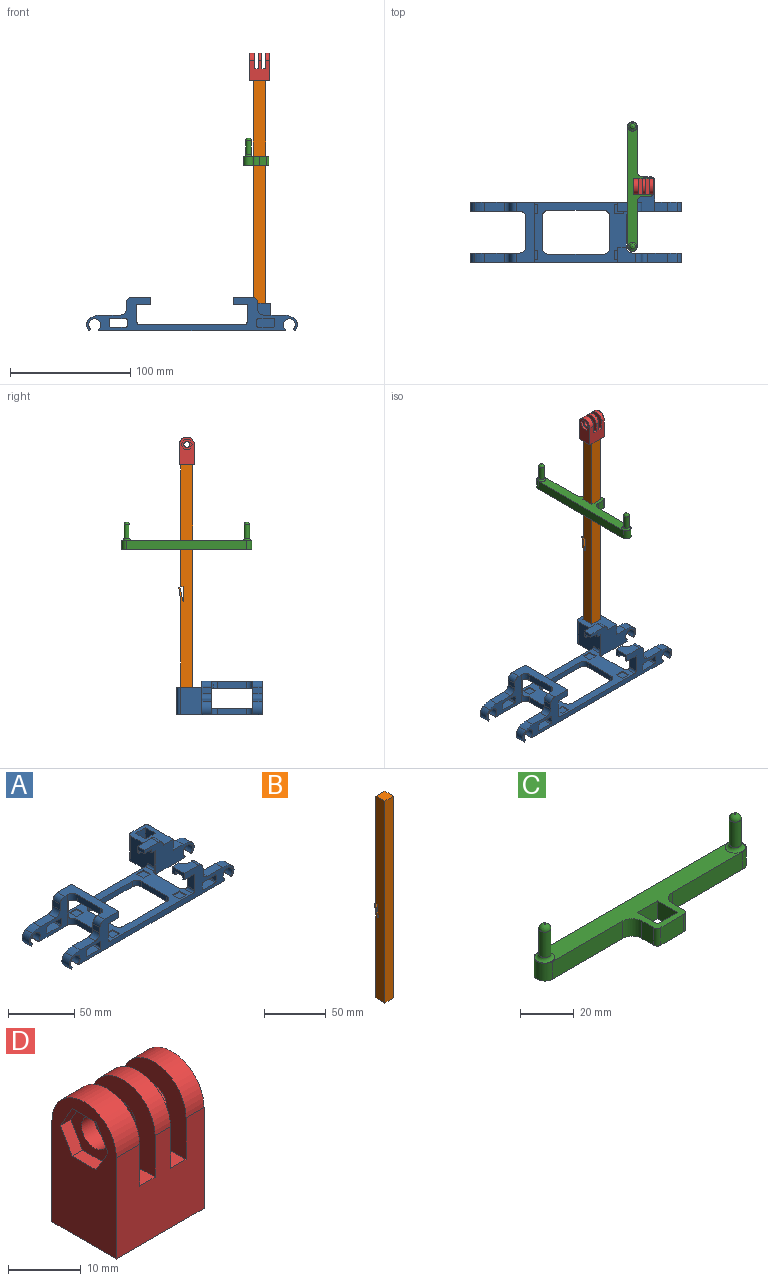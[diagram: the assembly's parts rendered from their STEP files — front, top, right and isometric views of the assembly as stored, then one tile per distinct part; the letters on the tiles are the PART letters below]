
ASSEMBLY  parts=4 mates=3
PART A: 147 faces, bbox 175.5x70.9x28.2 mm
  f0: plane 15x12.6mm, normal (0,0,1), area 154.4mm2, adj f4,f5,f6,f66,f114,f146
  f1: plane 15x7.6mm, normal (0,0,1), area 114mm2, adj f30,f61,f65,f115
  f2: plane 11x7.6mm, normal (0,0,-1), area 39.7mm2, adj f30,f55,f61,f65,f103,f104
  f3: plane 12.6x11mm, normal (0,0,-1), area 67.7mm2, adj f4,f5,f47,f66,f99,f100,f101,f146
  f4: plane 12.6x6mm, normal (-1,0,0), area 53.1mm2, adj f0,f3,f5,f100,f101,f102,f146
  f5: plane 175.5x28.17mm, normal (0,-1,0), area 1536.8mm2, adj f0,f3,f4,f7,f11,f12,f13,f14
  f6: plane 40.95x28.17mm, normal (0,1,0), area 444.6mm2, adj f0,f19,f45,f48,f49,f50,f51,f52
  f7: plane 87.6x50mm, normal (0,0,1), area 2008.8mm2, adj f5,f9,f12,f23,f34,f35,f36,f37
  f8: plane 10.5x7.6mm, normal (0,0,1), area 79.8mm2, adj f10,f56,f65,f69
  f9: plane 133.55x28.17mm, normal (0,1,0), area 998.3mm2, adj f7,f19,f21,f22,f23,f24,f25,f26
  f10: plane 22.25x13.17mm, normal (0,1,0), area 185.6mm2, adj f8,f19,f56,f57,f58,f59,f60,f69
  f11: plane 16.2x7.6mm, normal (0,0,1), area 123.1mm2, adj f5,f14,f39,f117
  f12: cylinder r=2mm len=8.6mm, axis (0,1,0), area 25mm2, adj f5,f7,f13,f41
  f13: plane 15x7.7mm, normal (1,0,0), area 115.5mm2, adj f5,f12,f32,f41
  f14: cylinder r=17.38mm len=8.18mm, axis (0,1,0), area 64.7mm2, adj f5,f11,f15,f39
  f15: cylinder r=6.75mm len=11.13mm, axis (0,1,0), area 100.2mm2, adj f5,f14,f16,f39
  f16: plane 7.6x1.34mm, normal (0.77,0,-0.64), area 13.3mm2, adj f5,f15,f17,f39
  f17: cylinder r=5mm len=10mm, axis (0,1,0), area 189mm2, adj f5,f16,f18,f39
  f18: plane 7.6x0.9mm, normal (-0.82,0,-0.57), area 8.4mm2, adj f5,f17,f19,f39
  f19: plane 155x70.9mm, normal (0,0,-1), area 3670mm2, adj f5,f6,f9,f10,f18,f29,f34,f35
  f20: plane 7.6x5mm, normal (-1,0,0), area 38mm2, adj f5,f39,f117,f118
  f21: plane 50x15mm, normal (0,0,1), area 482.3mm2, adj f5,f9,f33,f39,f40,f41,f43,f44
  f22: plane 16.2x7.6mm, normal (0,0,1), area 123.1mm2, adj f9,f25,f40,f120
  f23: cylinder r=2mm len=8.6mm, axis (0,1,0), area 25mm2, adj f7,f9,f24,f44
  f24: plane 15x7.7mm, normal (1,0,0), area 115.5mm2, adj f9,f23,f32,f44
  f25: cylinder r=17.38mm len=8.18mm, axis (0,1,0), area 64.7mm2, adj f9,f22,f26,f40
  f26: cylinder r=6.75mm len=11.13mm, axis (0,1,0), area 100.2mm2, adj f9,f25,f27,f40
  f27: plane 7.6x1.34mm, normal (0.77,0,-0.64), area 13.3mm2, adj f9,f26,f28,f40
  f28: cylinder r=5mm len=10mm, axis (0,1,0), area 189mm2, adj f9,f27,f29,f40
  f29: plane 7.6x0.9mm, normal (-0.82,0,-0.57), area 8.4mm2, adj f9,f19,f28,f40
  f30: plane 20x6mm, normal (0,1,0), area 105.6mm2, adj f1,f2,f55,f61,f77,f115
  f31: plane 7.6x5mm, normal (-1,0,0), area 38mm2, adj f9,f40,f119,f120
  f32: plane 50x11mm, normal (0,0,-1), area 309mm2, adj f5,f9,f13,f24,f33,f41,f43,f44
  f33: plane 50x6mm, normal (1,0,0), area 255mm2, adj f5,f9,f21,f32,f106,f107,f109,f111
  f34: cylinder r=5mm len=5mm, axis (0,0,1), area 39.3mm2, adj f7,f19,f35,f38
  f35: plane 45.6x5mm, normal (0,1,0), area 228mm2, adj f7,f19,f34,f62
  f36: plane 45.6x5mm, normal (0,-1,0), area 228mm2, adj f7,f19,f37,f63
  f37: cylinder r=5mm len=5mm, axis (0,0,1), area 39.3mm2, adj f7,f19,f36,f38
  f38: plane 26.8x5mm, normal (1,0,0), area 134mm2, adj f7,f19,f34,f37
  f39: plane 40.95x28.17mm, normal (0,1,0), area 444.6mm2, adj f11,f14,f15,f16,f17,f18,f19,f20
  f40: plane 40.95x28.17mm, normal (0,-1,0), area 444.6mm2, adj f19,f21,f22,f25,f26,f27,f28,f29
  f41: cylinder r=5mm len=28mm, axis (0,0,1), area 104.4mm2, adj f7,f12,f13,f19,f21,f32,f39,f42
  f42: plane 24.8x5mm, normal (-1,0,0), area 124mm2, adj f7,f19,f41,f44
  f43: plane 24.8x6mm, normal (-1,0,0), area 148.8mm2, adj f21,f32,f41,f44
  f44: cylinder r=5mm len=28mm, axis (0,0,1), area 104.4mm2, adj f7,f19,f21,f23,f24,f32,f40,f42
  f45: plane 16.2x7.6mm, normal (0,0,1), area 123.1mm2, adj f5,f6,f48,f116
  f46: cylinder r=2mm len=8.6mm, axis (0,1,0), area 25mm2, adj f5,f7,f47,f66
  f47: plane 15x7.7mm, normal (-1,0,0), area 115.5mm2, adj f3,f5,f46,f66
  f48: cylinder r=17.38mm len=8.18mm, axis (0,1,0), area 64.7mm2, adj f5,f6,f45,f49
  f49: cylinder r=6.75mm len=11.13mm, axis (0,1,0), area 100.2mm2, adj f5,f6,f48,f50
  f50: plane 7.6x1.34mm, normal (-0.77,0,-0.64), area 13.3mm2, adj f5,f6,f49,f51
  f51: cylinder r=5mm len=10mm, axis (0,1,0), area 189mm2, adj f5,f6,f50,f52
  f52: plane 7.6x0.9mm, normal (0.82,0,-0.57), area 8.4mm2, adj f5,f6,f19,f51
  f53: plane 7.6x5mm, normal (1,0,0), area 38mm2, adj f5,f6,f114,f116
  f54: cylinder r=2mm len=8.6mm, axis (0,1,0), area 25mm2, adj f7,f9,f55,f68
  f55: plane 25.6x23mm, normal (-1,0,0), area 527.2mm2, adj f2,f9,f19,f30,f54,f68,f72,f77
  f56: cylinder r=17.38mm len=8.18mm, axis (0,1,0), area 64.7mm2, adj f8,f10,f57,f65
  f57: cylinder r=6.75mm len=11.13mm, axis (0,1,0), area 100.2mm2, adj f10,f56,f58,f65
  f58: plane 7.6x1.34mm, normal (-0.77,0,-0.64), area 13.3mm2, adj f10,f57,f59,f65
  f59: cylinder r=5mm len=10mm, axis (0,1,0), area 189mm2, adj f10,f58,f60,f65
  f60: plane 7.6x0.9mm, normal (0.82,0,-0.57), area 8.4mm2, adj f10,f19,f59,f65
  f61: plane 7.6x6mm, normal (-1,0,0), area 28.1mm2, adj f1,f2,f30,f65,f104,f105
  f62: cylinder r=5mm len=5mm, axis (0,0,1), area 39.3mm2, adj f7,f19,f35,f64
  f63: cylinder r=5mm len=5mm, axis (0,0,1), area 39.3mm2, adj f7,f19,f36,f64
  f64: plane 26.8x5mm, normal (-1,0,0), area 134mm2, adj f7,f19,f62,f63
  f65: plane 52.95x28.17mm, normal (0,-1,0), area 699.8mm2, adj f1,f2,f8,f19,f56,f57,f58,f59
  f66: cylinder r=5mm len=28mm, axis (0,0,1), area 104.4mm2, adj f0,f3,f6,f7,f19,f46,f47,f67
  f67: plane 24.8x5mm, normal (1,0,0), area 124mm2, adj f7,f19,f66,f68
  f68: cylinder r=5mm len=22mm, axis (0,0,1), area 57.3mm2, adj f7,f19,f54,f55,f65,f67,f145
  f69: plane 25.5x23mm, normal (1,0,0), area 487.7mm2, adj f8,f10,f19,f65,f70,f77
  f70: cylinder r=3mm len=23mm, axis (0,0,1), area 108.4mm2, adj f19,f69,f71,f77
  f71: plane 23x13.7mm, normal (0,1,0), area 315.1mm2, adj f19,f70,f72,f77
  f72: cylinder r=3mm len=23mm, axis (0,0,1), area 108.4mm2, adj f19,f55,f71,f77
  f73: plane 10.5x10mm, normal (0,1,0), area 105mm2, adj f74,f76,f77,f78
  f74: plane 10.5x10mm, normal (1,0,0), area 105mm2, adj f73,f75,f77,f78
  f75: plane 10.5x10mm, normal (0,-1,0), area 105mm2, adj f74,f76,f77,f78
  f76: plane 10.5x10mm, normal (-1,0,0), area 105mm2, adj f73,f75,f77,f78
  f77: plane 28.5x19.7mm, normal (0,0,1), area 378.9mm2, adj f30,f55,f65,f69,f70,f71,f72,f73
  f78: plane 10.5x10.5mm, normal (0,0,1), area 110.3mm2, adj f73,f74,f75,f76
  f79: plane 7.5x1mm, normal (-1,0,0), area 7.5mm2, adj f7,f80,f82,f83
  f80: plane 7.5x1mm, normal (0,-1,0), area 7.5mm2, adj f7,f79,f81,f83
  f81: plane 7.5x1mm, normal (1,0,0), area 7.5mm2, adj f7,f80,f82,f83
  f82: plane 7.5x1mm, normal (0,1,0), area 7.5mm2, adj f7,f79,f81,f83
  f83: plane 7.5x7.5mm, normal (0,0,1), area 56.2mm2, adj f79,f80,f81,f82
  f84: plane 7.5x1mm, normal (1,0,0), area 7.5mm2, adj f7,f85,f87,f88
  f85: plane 7.5x1mm, normal (0,1,0), area 7.5mm2, adj f7,f84,f86,f88
  f86: plane 7.5x1mm, normal (-1,0,0), area 7.5mm2, adj f7,f85,f87,f88
  f87: plane 7.5x1mm, normal (0,-1,0), area 7.5mm2, adj f7,f84,f86,f88
  f88: plane 7.5x7.5mm, normal (0,0,1), area 56.2mm2, adj f84,f85,f86,f87
  f89: plane 7.5x1mm, normal (0,1,0), area 7.5mm2, adj f7,f90,f92,f93
  f90: plane 7.5x1mm, normal (-1,0,0), area 7.5mm2, adj f7,f89,f91,f93
  f91: plane 7.5x1mm, normal (0,-1,0), area 7.5mm2, adj f7,f90,f92,f93
  f92: plane 7.5x1mm, normal (1,0,0), area 7.5mm2, adj f7,f89,f91,f93
  f93: plane 7.5x7.5mm, normal (0,0,1), area 56.3mm2, adj f89,f90,f91,f92
  f94: plane 7.5x1mm, normal (1,0,0), area 7.5mm2, adj f7,f95,f97,f98
  f95: plane 7.5x1mm, normal (0,1,0), area 7.5mm2, adj f7,f94,f96,f98
  f96: plane 7.5x1mm, normal (-1,0,0), area 7.5mm2, adj f7,f95,f97,f98
  f97: plane 7.5x1mm, normal (0,-1,0), area 7.5mm2, adj f7,f94,f96,f98
  f98: plane 7.5x7.5mm, normal (0,0,1), area 56.2mm2, adj f94,f95,f96,f97
  f99: plane 7.5x3mm, normal (-1,0,0), area 22.5mm2, adj f3,f100,f101,f102
  f100: plane 7.5x3mm, normal (0,-1,0), area 22.5mm2, adj f3,f4,f99,f102
  f101: plane 7.5x3mm, normal (0,1,0), area 22.5mm2, adj f3,f4,f99,f102
  f102: plane 7.5x7.5mm, normal (0,0,-1), area 56.2mm2, adj f4,f99,f100,f101
  f103: plane 5.85x3mm, normal (-1,0,0), area 17.6mm2, adj f2,f65,f104,f105
  f104: plane 7.5x3mm, normal (0,-1,0), area 22.5mm2, adj f2,f61,f103,f105
  f105: plane 7.5x5.85mm, normal (0,0,-1), area 43.9mm2, adj f61,f65,f103,f104
  f106: plane 7.5x3mm, normal (0,1,0), area 22.5mm2, adj f32,f33,f108,f109
  f107: plane 7.5x3mm, normal (0,-1,0), area 22.5mm2, adj f32,f33,f108,f109
  f108: plane 7.5x3mm, normal (1,0,0), area 22.5mm2, adj f32,f106,f107,f109
  f109: plane 7.5x7.5mm, normal (0,0,-1), area 56.2mm2, adj f33,f106,f107,f108
  f110: plane 7.5x3mm, normal (1,0,0), area 22.5mm2, adj f32,f111,f112,f113
  f111: plane 7.5x3mm, normal (0,1,0), area 22.5mm2, adj f32,f33,f110,f113
  f112: plane 7.5x3mm, normal (0,-1,0), area 22.5mm2, adj f32,f33,f110,f113
  f113: plane 7.5x7.5mm, normal (0,0,-1), area 56.2mm2, adj f33,f110,f111,f112
  f114: cylinder r=5mm len=7.6mm, axis (0,-1,0), area 59.7mm2, adj f0,f5,f6,f53
  f115: cylinder r=5mm len=7.6mm, axis (0,-1,0), area 59.7mm2, adj f1,f30,f65,f77
  f116: cylinder r=5mm len=7.6mm, axis (0,-1,0), area 59.7mm2, adj f5,f6,f45,f53
  f117: cylinder r=5mm len=7.6mm, axis (0,-1,0), area 59.7mm2, adj f5,f11,f20,f39
  f118: cylinder r=5mm len=7.6mm, axis (0,-1,0), area 59.7mm2, adj f5,f20,f21,f39
  f119: cylinder r=5mm len=7.6mm, axis (0,-1,0), area 59.7mm2, adj f9,f21,f31,f40
  f120: cylinder r=5mm len=7.6mm, axis (0,-1,0), area 59.7mm2, adj f9,f22,f31,f40
  f121: plane 7.6x5mm, normal (1,0,0), area 38mm2, adj f9,f40,f122,f128
  f122: cylinder r=1mm len=7.6mm, axis (0,-1,0), area 11.9mm2, adj f9,f40,f121,f123
  f123: plane 13x7.6mm, normal (0,0,-1), area 98.8mm2, adj f9,f40,f122,f124
  f124: cylinder r=1mm len=7.6mm, axis (0,-1,0), area 11.9mm2, adj f9,f40,f123,f125
  f125: plane 7.6x5mm, normal (-1,0,0), area 38mm2, adj f9,f40,f124,f126
  f126: cylinder r=1mm len=7.6mm, axis (0,-1,0), area 11.9mm2, adj f9,f40,f125,f127
  f127: plane 13x7.6mm, normal (0,0,1), area 98.8mm2, adj f9,f40,f126,f128
  f128: cylinder r=1mm len=7.6mm, axis (0,-1,0), area 11.9mm2, adj f9,f40,f121,f127
  f129: cylinder r=1mm len=7.6mm, axis (0,-1,0), area 11.9mm2, adj f5,f39,f130,f136
  f130: plane 13x7.6mm, normal (0,0,1), area 98.8mm2, adj f5,f39,f129,f131
  f131: cylinder r=1mm len=7.6mm, axis (0,-1,0), area 11.9mm2, adj f5,f39,f130,f132
  f132: plane 7.6x5mm, normal (-1,0,0), area 38mm2, adj f5,f39,f131,f133
  f133: cylinder r=1mm len=7.6mm, axis (0,-1,0), area 11.9mm2, adj f5,f39,f132,f134
  f134: plane 13x7.6mm, normal (0,0,-1), area 98.8mm2, adj f5,f39,f133,f135
  f135: cylinder r=1mm len=7.6mm, axis (0,-1,0), area 11.9mm2, adj f5,f39,f134,f136
  f136: plane 7.6x5mm, normal (1,0,0), area 38mm2, adj f5,f39,f129,f135
  f137: plane 13x7.6mm, normal (0,0,1), area 98.8mm2, adj f5,f6,f138,f142
  f138: cylinder r=1mm len=7.6mm, axis (0,-1,0), area 11.9mm2, adj f5,f6,f137,f139
  f139: plane 7.6x5mm, normal (-1,0,0), area 38mm2, adj f5,f6,f138,f140
  f140: cylinder r=1mm len=7.6mm, axis (0,-1,0), area 11.9mm2, adj f5,f6,f139,f141
  f141: plane 13x7.6mm, normal (0,0,-1), area 98.8mm2, adj f5,f6,f140,f143
  f142: cylinder r=1mm len=7.6mm, axis (0,-1,0), area 11.9mm2, adj f5,f6,f137,f144
  f143: cylinder r=1mm len=7.6mm, axis (0,-1,0), area 11.9mm2, adj f5,f6,f141,f144
  f144: plane 7.6x5mm, normal (1,0,0), area 38mm2, adj f5,f6,f142,f143
  f145: plane 1x0.1mm, normal (0,0,1), area 0mm2, adj f55,f65,f68
  f146: plane 7x6mm, normal (0,1,0), area 42mm2, adj f0,f3,f4,f66
PART B: 13 faces, bbox 10.1x11.8x200 mm
  f0: plane 81.12x10.1mm, normal (0,1,0), area 819.3mm2, adj f1,f2,f6,f12
  f1: plane 200x11.77mm, normal (1,0,0), area 2009.3mm2, adj f0,f3,f4,f5,f6,f7,f8,f9
  f2: plane 200x11.77mm, normal (-1,0,0), area 2009.3mm2, adj f0,f3,f4,f5,f6,f7,f8,f9
  f3: plane 200x10.1mm, normal (0,-1,0), area 2020mm2, adj f1,f2,f5,f6
  f4: plane 106.39x10.1mm, normal (0,1,0), area 1074.5mm2, adj f1,f2,f5,f9
  f5: plane 10.1x10.1mm, normal (0,0,1), area 102mm2, adj f1,f2,f3,f4
  f6: plane 10.1x10.1mm, normal (0,0,-1), area 102mm2, adj f0,f1,f2,f3
  f7: plane 11.88x10.1mm, normal (0,-0.98,0.22), area 123mm2, adj f1,f2,f8,f11
  f8: plane 10.1x0.5mm, normal (0,0,1), area 5.1mm2, adj f1,f2,f7,f10
  f9: plane 10.1x2.06mm, normal (0,0,-1), area 20.8mm2, adj f1,f2,f4,f10
  f10: plane 12.49x10.1mm, normal (0,1,-0.03), area 126.3mm2, adj f1,f2,f8,f9
  f11: plane 10.1x1mm, normal (0,0,1), area 10.1mm2, adj f1,f2,f7,f12
  f12: plane 11.88x10.1mm, normal (0,0.99,-0.14), area 121.2mm2, adj f0,f1,f2,f11
PART C: 26 faces, bbox 110.4x22.2x23 mm
  f0: plane 10.5x8mm, normal (1,0,0), area 84mm2, adj f1,f15,f16,f17
  f1: plane 10.5x8mm, normal (0,-1,0), area 84mm2, adj f0,f2,f16,f17
  f2: plane 10.5x8mm, normal (-1,0,0), area 84mm2, adj f1,f15,f16,f17
  f3: plane 100x8mm, normal (0,1,0), area 800mm2, adj f4,f14,f16,f17
  f4: cylinder r=4mm len=8mm, axis (0,0,1), area 100.5mm2, adj f3,f5,f16,f17
  f5: plane 37x8mm, normal (0,-1,0), area 296mm2, adj f4,f6,f16,f17
  f6: cylinder r=5mm len=8mm, axis (0,0,1), area 62.8mm2, adj f5,f7,f16,f17
  f7: plane 8x6mm, normal (-1,0,0), area 48mm2, adj f6,f8,f16,f17
  f8: cylinder r=2mm len=8mm, axis (0,0,1), area 25.1mm2, adj f7,f9,f16,f17
  f9: plane 12x8mm, normal (0,-1,0), area 96mm2, adj f8,f10,f16,f17
  f10: cylinder r=2mm len=8mm, axis (0,0,1), area 25.1mm2, adj f9,f11,f16,f17
  f11: plane 8x6mm, normal (1,0,0), area 48mm2, adj f10,f12,f16,f17
  f12: cylinder r=5mm len=8mm, axis (0,0,1), area 62.8mm2, adj f11,f13,f16,f17
  f13: plane 37x8mm, normal (0,-1,0), area 296mm2, adj f12,f14,f16,f17
  f14: cylinder r=4mm len=8mm, axis (0,0,1), area 100.5mm2, adj f3,f13,f16,f17
  f15: plane 10.5x8mm, normal (0,1,0), area 84mm2, adj f0,f2,f16,f17
  f16: plane 108x21mm, normal (0,0,-1), area 957mm2, adj f0,f1,f2,f3,f4,f5,f6,f7
  f17: plane 108x21mm, normal (0,0,1), area 868.7mm2, adj f0,f1,f2,f3,f4,f5,f6,f7
  f18: cylinder r=2.25mm len=11.5mm, axis (0,0,-1), area 162.6mm2, adj f23,f25
  f19: plane 0.5x0.5mm, normal (0,0,1), area 0.2mm2, adj f25
  f20: cylinder r=2.25mm len=11.5mm, axis (0,0,-1), area 162.6mm2, adj f22,f24
  f21: plane 0.5x0.5mm, normal (0,0,1), area 0.2mm2, adj f24
  f22: torus R=3.75mm, axis (0,0,1), area 41.4mm2, adj f17,f20
  f23: torus R=3.75mm, axis (0,0,1), area 41.4mm2, adj f17,f18
  f24: torus R=0.25mm, axis (0,0,1), area 30.1mm2, adj f20,f21
  f25: torus R=0.25mm, axis (0,0,1), area 30.1mm2, adj f18,f19
PART D: 29 faces, bbox 17x12.5x23.3 mm
  f0: cylinder r=6.25mm len=12.5mm, axis (-1,0,0), area 58.9mm2, adj f3,f5,f17,f22
  f1: cylinder r=6.25mm len=12.5mm, axis (-1,0,0), area 68.7mm2, adj f3,f5,f7,f18
  f2: cylinder r=2.5mm len=5mm, axis (-1,0,0), area 55mm2, adj f7,f18
  f3: plane 17x17mm, normal (0,1,0), area 247mm2, adj f0,f1,f4,f7,f8,f16,f17,f18
  f4: cylinder r=6.25mm len=12.5mm, axis (-1,0,0), area 88.4mm2, adj f3,f5,f8,f21
  f5: plane 17x17mm, normal (0,-1,0), area 247mm2, adj f0,f1,f4,f7,f8,f16,f17,f18
  f6: cylinder r=2.5mm len=5mm, axis (-1,0,0), area 39.3mm2, adj f15,f21
  f7: plane 23.25x12.5mm, normal (1,0,0), area 254.2mm2, adj f1,f2,f3,f5,f27
  f8: plane 23.25x12.5mm, normal (-1,0,0), area 218.4mm2, adj f3,f4,f5,f9,f10,f11,f12,f13
  f9: plane 4x2.31mm, normal (0,-0.87,0.5), area 9.2mm2, adj f8,f10,f14,f15
  f10: plane 4x2.31mm, normal (0,-0.87,-0.5), area 9.2mm2, adj f8,f9,f11,f15
  f11: plane 4.62x2mm, normal (0,0,-1), area 9.2mm2, adj f8,f10,f12,f15
  f12: plane 4x2.31mm, normal (0,0.87,-0.5), area 9.2mm2, adj f8,f11,f13,f15
  f13: plane 4x2.31mm, normal (0,0.87,0.5), area 9.2mm2, adj f8,f12,f14,f15
  f14: plane 4.62x2mm, normal (0,0,1), area 9.2mm2, adj f8,f9,f13,f15
  f15: plane 9.24x8mm, normal (-1,0,0), area 35.8mm2, adj f6,f9,f10,f11,f12,f13,f14
  f16: plane 12.5x3mm, normal (0,0,1), area 37.5mm2, adj f3,f5,f17,f18
  f17: plane 13.25x12.5mm, normal (1,0,0), area 129.2mm2, adj f0,f3,f5,f16,f19
  f18: plane 13.25x12.5mm, normal (-1,0,0), area 129.2mm2, adj f1,f2,f3,f5,f16
  f19: cylinder r=2.5mm len=5mm, axis (-1,0,0), area 47.1mm2, adj f17,f22
  f20: plane 12.5x3mm, normal (0,0,1), area 37.5mm2, adj f3,f5,f21,f22
  f21: plane 13.25x12.5mm, normal (1,0,0), area 129.2mm2, adj f3,f4,f5,f6,f20
  f22: plane 13.25x12.5mm, normal (-1,0,0), area 129.2mm2, adj f0,f3,f5,f19,f20
  f23: plane 10.3x5mm, normal (0,-1,0), area 51.5mm2, adj f24,f26,f27,f28
  f24: plane 10.3x5mm, normal (1,0,0), area 51.5mm2, adj f23,f25,f27,f28
  f25: plane 10.3x5mm, normal (0,1,0), area 51.5mm2, adj f24,f26,f27,f28
  f26: plane 10.3x5mm, normal (-1,0,0), area 51.5mm2, adj f23,f25,f27,f28
  f27: plane 17x12.5mm, normal (0,0,-1), area 106.4mm2, adj f3,f5,f7,f8,f23,f24,f25,f26
  f28: plane 10.3x10.3mm, normal (0,0,-1), area 106.1mm2, adj f23,f24,f25,f26
PLACE A at identity fixed
PLACE B at identity
PLACE C rot(axis=(0,0,1),90deg) t=(47,12.65,140.3)mm
PLACE D at identity
MATE fastened B.f5 <-> D.f28  axis (0,0,1) through (56.25,12.65,208)mm
MATE slider C.f17 <-> B.f5  axis (0,0,1) through (56.25,12.65,140.3)mm
MATE fastened B.f6 <-> A.f78  axis (0,0,-1) through (56.25,12.65,8)mm
